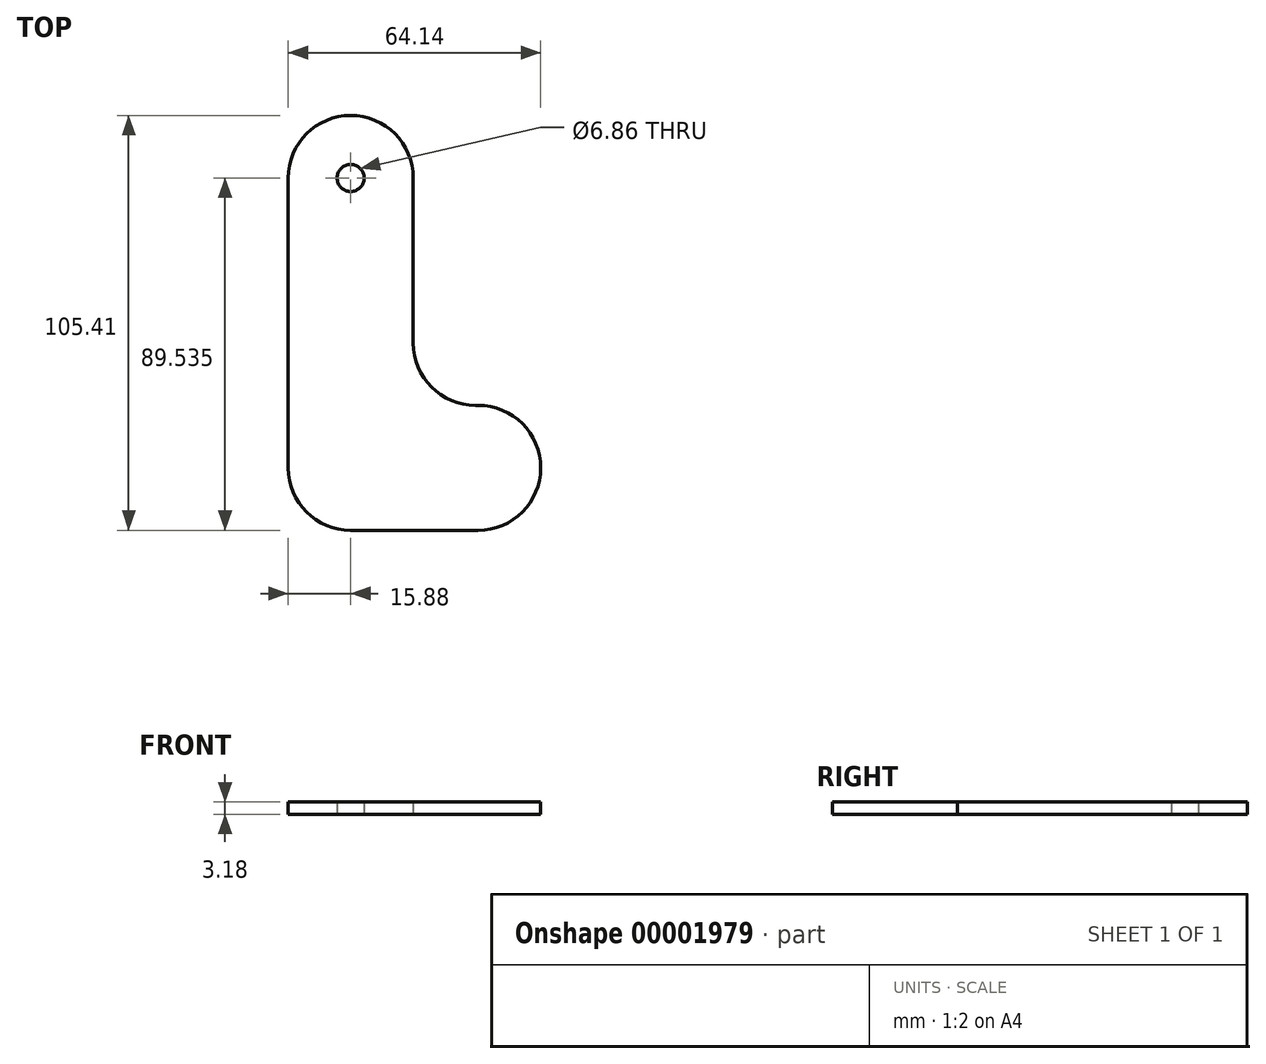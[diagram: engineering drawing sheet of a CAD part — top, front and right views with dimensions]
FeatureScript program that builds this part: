
annotation { "Feature Type Name" : "Feature", "Feature Type Description" : "" }
export const myFeature = defineFeature(function(context is Context, id is Id, definition is map)
    precondition{}
    {
        {
            var Q0;
            Q0=qCreatedBy(makeId("Top.planeOp"),FACE);
            var sketch = newSketch(context, id + "F0", { "sketchPlane" : qUnion([Q0])});
            skLineSegment(sketch, "E0.rect.bottom", {"start": v(48.26, -73.66) * mm, "end": v(-48.26, -73.66) * mm, "construction": true});
            skLineSegment(sketch, "E0.rect.top", {"start": v(48.26, 73.66) * mm, "end": v(-48.26, 73.66) * mm, "construction": true});
            skLineSegment(sketch, "E0.rect.left", {"start": v(48.26, -73.66) * mm, "end": v(48.26, 73.66) * mm, "construction": true});
            skLineSegment(sketch, "E0.rect.right", {"start": v(-48.26, -73.66) * mm, "end": v(-48.26, 73.66) * mm, "construction": true});
            skPoint(sketch, "E0.rect.middle", {"position": v(0, 0) * mm});
            skLineSegment(sketch, "E1.rect.top", {"start": v(5.94, 95.63) * mm, "end": v(-16.54, 95.63) * mm, "construction": true});
            skLineSegment(sketch, "E1.rect.right", {"start": v(-16.54, 83.44) * mm, "end": v(-16.54, 95.63) * mm, "construction": true});
            skLineSegment(sketch, "E2", {"start": v(-16.54, 89.53) * mm, "end": v(5.94, 89.53) * mm, "construction": true});
            skPoint(sketch, "E3", {"position": v(0, 89.53) * mm});
            skLineSegment(sketch, "E4", {"start": v(48.26, 108.46) * mm, "end": v(-89.78, 108.46) * mm, "construction": true});
            skLineSegment(sketch, "E5.rect.left", {"start": v(15.88, 47.62) * mm, "end": v(15.88, 89.53) * mm});
            skLineSegment(sketch, "E5.rect.right", {"start": v(-15.88, 15.88) * mm, "end": v(-15.88, 89.54) * mm});
            skArc(sketch, "E6", {"start": v(15.87, 89.54) * mm, "mid": v(0, 105.41) * mm, "end": v(-15.88, 89.54) * mm});
            skLineSegment(sketch, "E7", {"start": v(5.94, 95.63) * mm, "end": v(5.94, 83.44) * mm, "construction": true});
            skLineSegment(sketch, "E8", {"start": v(5.94, 83.44) * mm, "end": v(-16.54, 83.44) * mm, "construction": true});
            skLineSegment(sketch, "E9.0.MirrorCS", {"start": v(5.94, -83.44) * mm, "end": v(-16.54, -83.44) * mm, "construction": true});
            skLineSegment(sketch, "E10.0.MirrorCS", {"start": v(5.94, -95.63) * mm, "end": v(5.94, -83.44) * mm, "construction": true});
            skLineSegment(sketch, "E11.0.MirrorCS", {"start": v(5.94, -95.63) * mm, "end": v(-16.54, -95.63) * mm, "construction": true});
            skLineSegment(sketch, "E12.0.MirrorCS", {"start": v(-16.54, -83.44) * mm, "end": v(-16.54, -95.63) * mm, "construction": true});
            skArc(sketch, "E13", {"start": v(-15.88, 89.54) * mm, "mid": v(0, 73.66) * mm, "end": v(15.88, 89.54) * mm, "construction": true});
            skCircle(sketch, "E14", {"center": v(0, 89.53) * mm, "radius": 3.43 * mm});
            skArc(sketch, "E15", {"start": v(32.38, 0) * mm, "mid": v(48.26, 15.88) * mm, "end": v(32.38, 31.75) * mm});
            skLineSegment(sketch, "E16", {"start": v(32.38, 31.75) * mm, "end": v(31.75, 31.75) * mm});
            skLineSegment(sketch, "E17", {"start": v(32.38, 0) * mm, "end": v(0, 0) * mm});
            skArc(sketch, "E18", {"start": v(-15.88, 15.87) * mm, "mid": v(-11.23, 4.65) * mm, "end": v(0, 0) * mm});
            skPoint(sketch, "E19.visualSharp", {"position": v(15.88, 31.75) * mm});
            skArc(sketch, "E19.filletArc", {"start": v(15.88, 47.62) * mm, "mid": v(20.52, 36.4) * mm, "end": v(31.75, 31.75) * mm});
            skSolve(sketch);
        }
        {
            var Q0;
            Q0=makeQuery(id+"F0.imprint","IMPRINT",FACE,{"disambiguationData":[TD([[makeQuery(id+"F0.imprint","IMPRINT",EDGE,{"derivedFrom":sQuery(id+"F0.wireOp",EDGE,"E5.rect.left")}),1.0]])]});
            var Q1;
            {var subQ1=sQuery(id+"F0.wireOp",EDGE,"98986e26-8f40-45f1-b6f0-e08adceff56f");Q1=makeQuery(id+"F0.imprint","IMPRINT",FACE,{"disambiguationData":[TD([[makeQuery(id+"F0.imprint","IMPRINT",EDGE,{"derivedFrom":subQ1}),-1.0]])]});}
            extrude(context, id + "F1", {"entities" : qUnion([Q0, Q1]), "depth" : 3.17 * mm});
        }
    });
